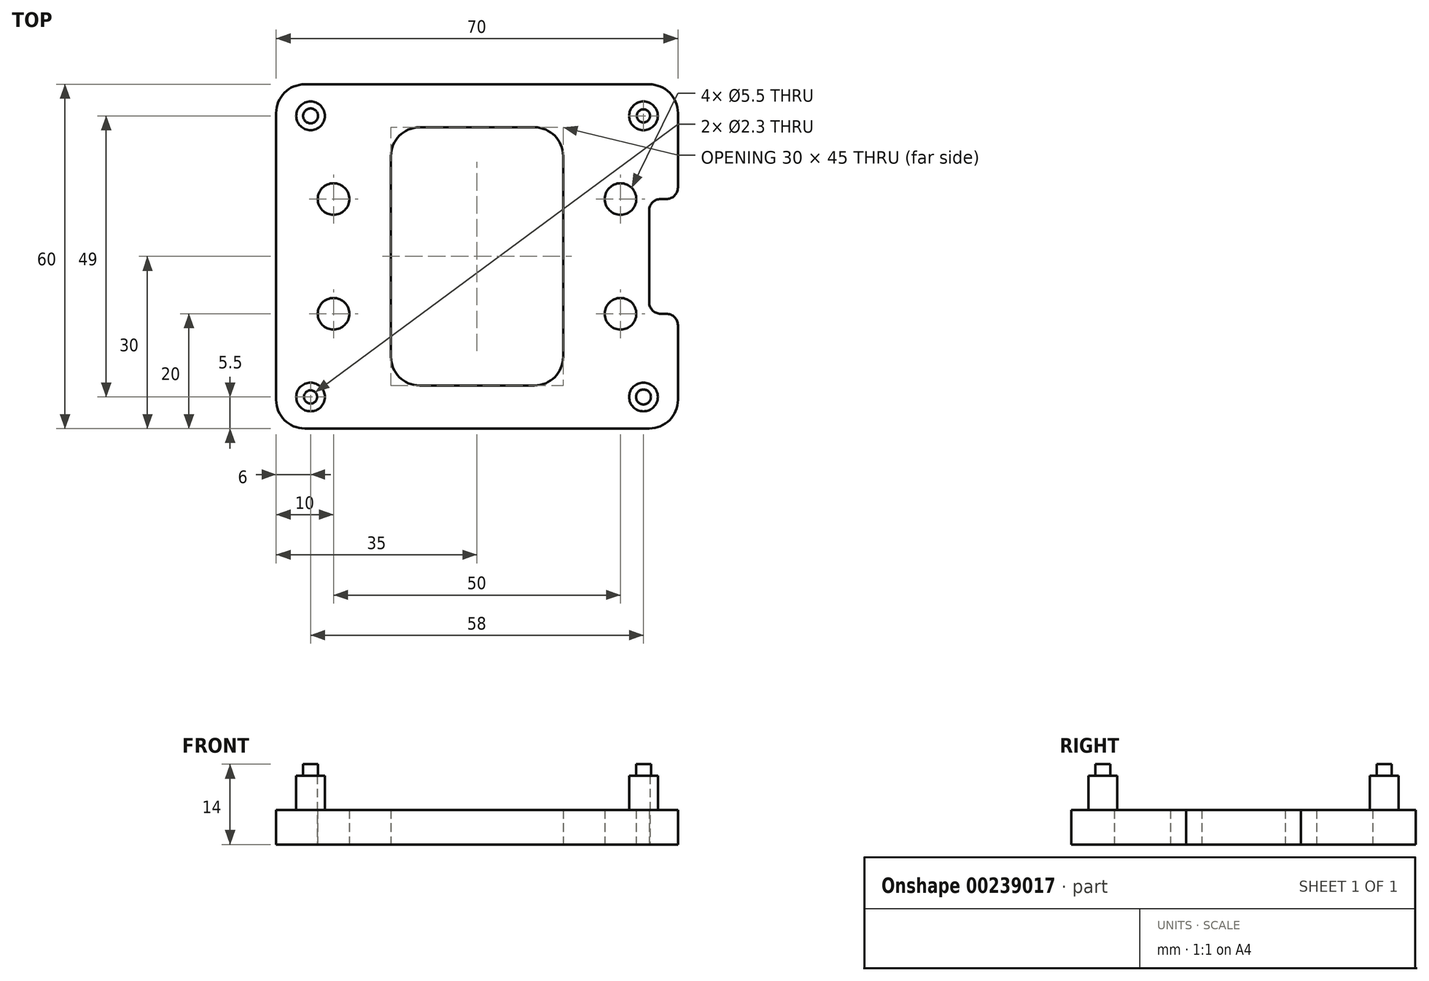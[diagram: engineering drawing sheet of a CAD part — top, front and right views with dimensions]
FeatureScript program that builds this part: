
annotation { "Feature Type Name" : "Feature", "Feature Type Description" : "" }
export const myFeature = defineFeature(function(context is Context, id is Id, definition is map)
    precondition{}
    {
        {
            var Q0;
            Q0=qCreatedBy(makeId("Top.planeOp"),FACE);
            var sketch = newSketch(context, id + "F0", { "sketchPlane" : qUnion([Q0])});
            skCircle(sketch, "E0", {"center": v(29, 24.5) * mm, "radius": 1.15 * mm});
            skCircle(sketch, "E1", {"center": v(-29, -24.5) * mm, "radius": 1.15 * mm});
            skLineSegment(sketch, "E2.bottom", {"start": v(-35, 30) * mm, "end": v(35, 30) * mm});
            skLineSegment(sketch, "E2.top", {"start": v(-35, -30) * mm, "end": v(35, -30) * mm});
            skLineSegment(sketch, "E2.left", {"start": v(-35, 30) * mm, "end": v(-35, -30) * mm});
            skCircle(sketch, "E3", {"center": v(-25, 10) * mm, "radius": 2.75 * mm});
            skCircle(sketch, "E4", {"center": v(-25, -10) * mm, "radius": 2.75 * mm});
            skCircle(sketch, "E5", {"center": v(25, -10) * mm, "radius": 2.75 * mm});
            skCircle(sketch, "E6", {"center": v(25, 10) * mm, "radius": 2.75 * mm});
            skLineSegment(sketch, "E7.bottom", {"start": v(-15, 22.5) * mm, "end": v(15, 22.5) * mm});
            skLineSegment(sketch, "E7.top", {"start": v(-15, -22.5) * mm, "end": v(15, -22.5) * mm});
            skLineSegment(sketch, "E7.left", {"start": v(-15, 22.5) * mm, "end": v(-15, -22.5) * mm});
            skLineSegment(sketch, "E7.right", {"start": v(15, 22.5) * mm, "end": v(15, -22.5) * mm});
            skLineSegment(sketch, "E8", {"start": v(35, 30) * mm, "end": v(35, 10) * mm});
            skLineSegment(sketch, "E9", {"start": v(35, 10) * mm, "end": v(30, 10) * mm});
            skLineSegment(sketch, "E10", {"start": v(30, 10) * mm, "end": v(30, -10) * mm});
            skLineSegment(sketch, "E11", {"start": v(30, -10) * mm, "end": v(35, -10) * mm});
            skLineSegment(sketch, "E12", {"start": v(35, -10) * mm, "end": v(35, -30) * mm});
            skSolve(sketch);
        }
        {
            var Q0;
            Q0=makeQuery(id+"F0.imprint","IMPRINT",FACE,{"disambiguationData":[TD([[makeQuery(id+"F0.imprint","IMPRINT",EDGE,{"derivedFrom":sQuery(id+"F0.wireOp",EDGE,"PQ99B8Q3-b4Bl-xYfH-NQoI-jWO0QoOsiCie")}),-1.0]])]});
            var Q1;
            Q1=makeQuery(id+"F0.imprint","IMPRINT",FACE,{"disambiguationData":[TD([[makeQuery(id+"F0.imprint","IMPRINT",EDGE,{"derivedFrom":sQuery(id+"F0.wireOp",EDGE,"E0")}),-1.0]])]});
            extrude(context, id + "F1", {"entities" : qUnion([Q0, Q1]), "depth" : 6 * mm});
        }
        {
            var Q0;
            Q0=makeQuery(id+"F1.opExtrude","SWEPT_EDGE",EDGE,{"disambiguationData":[OSD([sQuery(id+"F0.wireOp",EDGE,"E2.top"),sQuery(id+"F0.wireOp",EDGE,"E2.left")])]});
            var Q1;
            Q1=makeQuery(id+"F1.opExtrude","SWEPT_EDGE",EDGE,{"disambiguationData":[OSD([sQuery(id+"F0.wireOp",EDGE,"E2.top"),sQuery(id+"F0.wireOp",EDGE,"E2.right")])]});
            var Q2;
            Q2=makeQuery(id+"F1.opExtrude","SWEPT_EDGE",EDGE,{"disambiguationData":[OSD([sQuery(id+"F0.wireOp",EDGE,"E2.bottom"),sQuery(id+"F0.wireOp",EDGE,"E2.right")])]});
            var Q3;
            Q3=makeQuery(id+"F1.opExtrude","SWEPT_EDGE",EDGE,{"disambiguationData":[OSD([sQuery(id+"F0.wireOp",EDGE,"E2.bottom"),sQuery(id+"F0.wireOp",EDGE,"E2.left")])]});
            var Q4;
            Q4=makeQuery(id+"F1.opExtrude","SWEPT_EDGE",EDGE,{"disambiguationData":[OSD([sQuery(id+"F0.wireOp",EDGE,"E7.bottom"),sQuery(id+"F0.wireOp",EDGE,"E7.left")])]});
            var Q5;
            Q5=makeQuery(id+"F1.opExtrude","SWEPT_EDGE",EDGE,{"disambiguationData":[OSD([sQuery(id+"F0.wireOp",EDGE,"E7.bottom"),sQuery(id+"F0.wireOp",EDGE,"E7.right")])]});
            var Q6;
            Q6=makeQuery(id+"F1.opExtrude","SWEPT_EDGE",EDGE,{"disambiguationData":[OSD([sQuery(id+"F0.wireOp",EDGE,"E7.top"),sQuery(id+"F0.wireOp",EDGE,"E7.right")])]});
            var Q7;
            Q7=makeQuery(id+"F1.opExtrude","SWEPT_EDGE",EDGE,{"disambiguationData":[OSD([sQuery(id+"F0.wireOp",EDGE,"E7.top"),sQuery(id+"F0.wireOp",EDGE,"E7.left")])]});
            fillet(context, id + "F2", {"entities" : qUnion([Q0, Q1, Q2, Q3, Q4, Q5, Q6, Q7]), "radius" : 5 * mm, "tangentPropagation" : true, "allowEdgeOverflow" : false});
        }
        {
            var Q0;
            Q0=makeQuery(id+"F1.opExtrude","CAP_FACE",FACE,{"disambiguationData":[OSD([sQuery(id+"F0.wireOp",EDGE,"E0"),sQuery(id+"F0.wireOp",EDGE,"E1"),sQuery(id+"F0.wireOp",EDGE,"E2.bottom"),sQuery(id+"F0.wireOp",EDGE,"E2.top"),sQuery(id+"F0.wireOp",EDGE,"E2.left"),sQuery(id+"F0.wireOp",EDGE,"E2.right"),sQuery(id+"F0.wireOp",EDGE,"E3"),sQuery(id+"F0.wireOp",EDGE,"E4"),sQuery(id+"F0.wireOp",EDGE,"E5"),sQuery(id+"F0.wireOp",EDGE,"E6"),sQuery(id+"F0.wireOp",EDGE,"E7.bottom"),sQuery(id+"F0.wireOp",EDGE,"E7.top"),sQuery(id+"F0.wireOp",EDGE,"E7.left"),sQuery(id+"F0.wireOp",EDGE,"E7.right")])],"isStart":false});
            var sketch = newSketch(context, id + "F3", { "sketchPlane" : qUnion([Q0])});
            skCircle(sketch, "E13", {"center": v(-29, 24.5) * mm, "radius": 1.3 * mm});
            skCircle(sketch, "E14", {"center": v(29, -24.5) * mm, "radius": 1.3 * mm});
            skSolve(sketch);
        }
        {
            var Q0;
            Q0=makeQuery(id+"F3.imprint","IMPRINT",FACE,{"disambiguationData":[TD([[makeQuery(id+"F3.imprint","IMPRINT",EDGE,{"derivedFrom":sQuery(id+"F3.wireOp",EDGE,"E13")}),-1.0]])]});
            var sketch = newSketch(context, id + "F4", { "sketchPlane" : qUnion([Q0])});
            skCircle(sketch, "E15", {"center": v(-29, 24.5) * mm, "radius": 2.5 * mm});
            skCircle(sketch, "E16", {"center": v(29, 24.5) * mm, "radius": 2.5 * mm});
            skCircle(sketch, "E17", {"center": v(29, -24.5) * mm, "radius": 2.5 * mm});
            skCircle(sketch, "E18", {"center": v(-29, -24.5) * mm, "radius": 2.5 * mm});
            skSolve(sketch);
        }
        {
            var Q0;
            Q0 = qSketchRegion(id + "F4", true);
            extrude(context, id + "F5", {"entities" : qUnion([Q0]), "operationType" : NewBodyOperationType.ADD, "depth" : 6 * mm});
        }
        {
            var Q0;
            Q0 = qSketchRegion(id + "F3", true);
            extrude(context, id + "F6", {"entities" : qUnion([Q0]), "operationType" : NewBodyOperationType.ADD, "depth" : 8 * mm});
        }
        {
            var Q0;
            Q0=makeQuery(id+"F5.opExtrude","CAP_FACE",FACE,{"disambiguationData":[OSD([sQuery(id+"F4.wireOp",EDGE,"E18")])],"isStart":false});
            var sketch = newSketch(context, id + "F7", { "sketchPlane" : qUnion([Q0])});
            skCircle(sketch, "E19", {"center": v(-29, -24.5) * mm, "radius": 1.15 * mm});
            skCircle(sketch, "E20", {"center": v(29, 24.5) * mm, "radius": 1.15 * mm});
            skSolve(sketch);
        }
        {
            var Q0;
            Q0=makeQuery(id+"F7.imprint","IMPRINT",FACE,{"disambiguationData":[TD([[makeQuery(id+"F7.imprint","IMPRINT",EDGE,{"derivedFrom":sQuery(id+"F7.wireOp",EDGE,"E19")}),1.0]])]});
            var Q1;
            Q1=makeQuery(id+"F7.imprint","IMPRINT",FACE,{"disambiguationData":[TD([[makeQuery(id+"F7.imprint","IMPRINT",EDGE,{"derivedFrom":sQuery(id+"F7.wireOp",EDGE,"E20")}),1.0]])]});
            extrude(context, id + "F8", {"entities" : qUnion([Q0, Q1]), "operationType" : NewBodyOperationType.REMOVE, "oppositeDirection" : true, "depth" : 25 * mm});
        }
        {
            var Q0;
            Q0=makeQuery(id+"F1.opExtrude","SWEPT_EDGE",EDGE,{"disambiguationData":[OSD([sQuery(id+"F0.wireOp",EDGE,"E8"),sQuery(id+"F0.wireOp",EDGE,"E9")])]});
            var Q1;
            Q1=makeQuery(id+"F1.opExtrude","SWEPT_EDGE",EDGE,{"disambiguationData":[OSD([sQuery(id+"F0.wireOp",EDGE,"E9"),sQuery(id+"F0.wireOp",EDGE,"E10")])]});
            var Q2;
            Q2=makeQuery(id+"F1.opExtrude","SWEPT_EDGE",EDGE,{"disambiguationData":[OSD([sQuery(id+"F0.wireOp",EDGE,"E10"),sQuery(id+"F0.wireOp",EDGE,"E11")])]});
            var Q3;
            Q3=makeQuery(id+"F1.opExtrude","SWEPT_EDGE",EDGE,{"disambiguationData":[OSD([sQuery(id+"F0.wireOp",EDGE,"E11"),sQuery(id+"F0.wireOp",EDGE,"E12")])]});
            fillet(context, id + "F9", {"entities" : qUnion([Q0, Q1, Q2, Q3]), "radius" : 2 * mm, "tangentPropagation" : true, "allowEdgeOverflow" : false});
        }
    });
